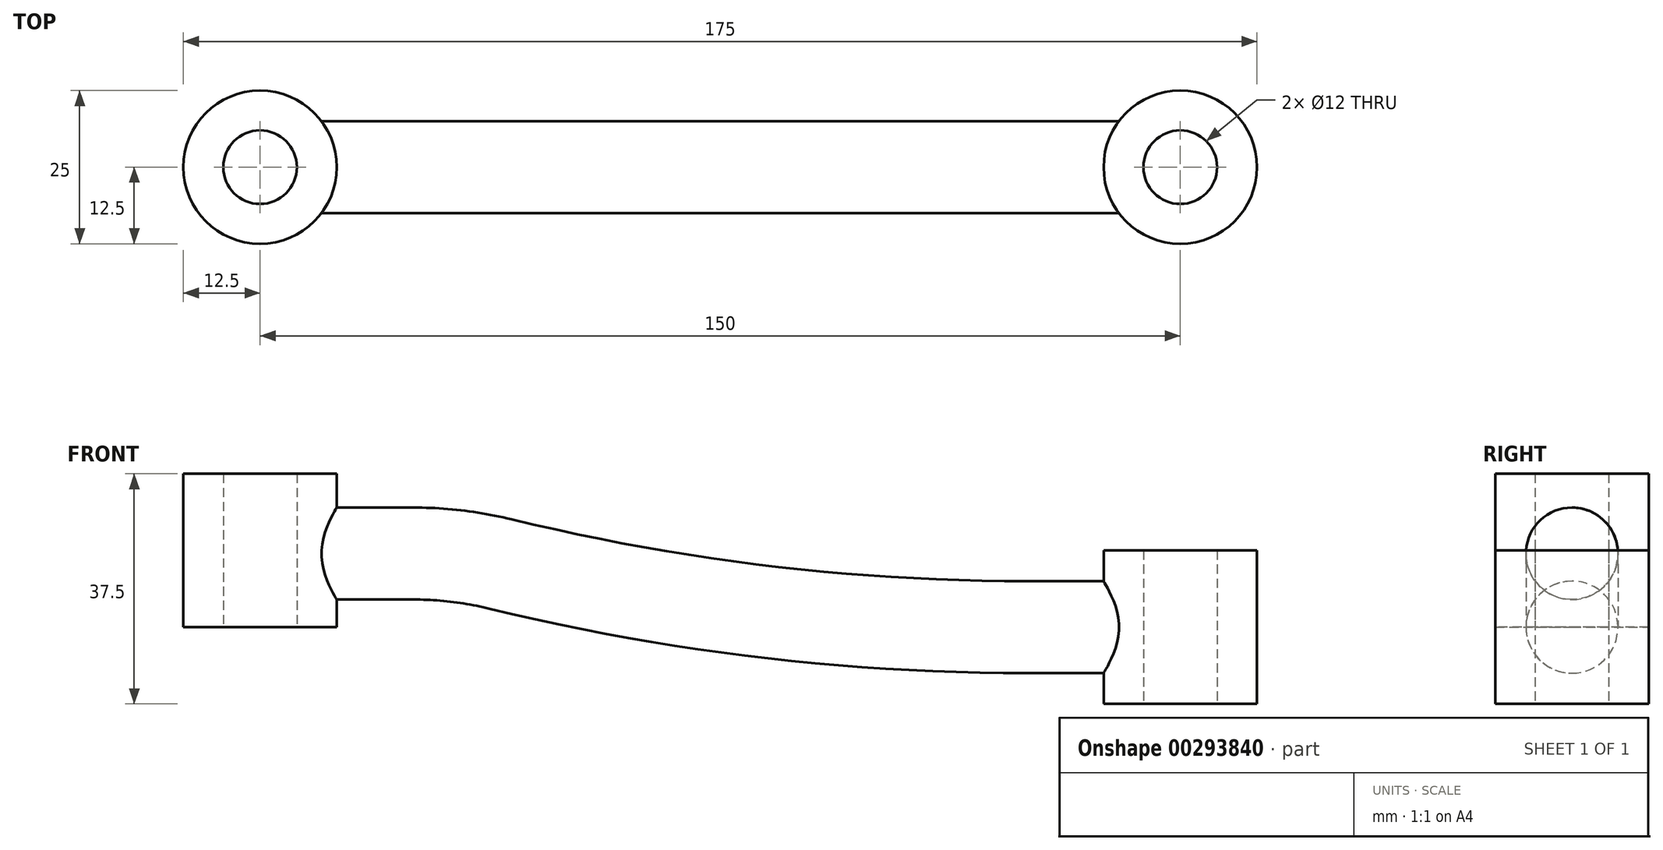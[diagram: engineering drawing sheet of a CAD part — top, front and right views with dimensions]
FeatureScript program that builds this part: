
annotation { "Feature Type Name" : "Feature", "Feature Type Description" : "" }
export const myFeature = defineFeature(function(context is Context, id is Id, definition is map)
    precondition{}
    {
        {
            var Q0;
            Q0=qCreatedBy(makeId("Top.planeOp"),FACE);
            var sketch = newSketch(context, id + "F0", { "sketchPlane" : qUnion([Q0])});
            skCircle(sketch, "E0", {"center": v(0, 0) * mm, "radius": 12.5 * mm});
            skCircle(sketch, "E1", {"center": v(150, 0) * mm, "radius": 12.5 * mm});
            skSolve(sketch);
        }
        {
            var Q0;
            Q0=makeQuery(id+"F0.imprint","IMPRINT",FACE,{"disambiguationData":[TD([[makeQuery(id+"F0.imprint","IMPRINT",EDGE,{"derivedFrom":sQuery(id+"F0.wireOp",EDGE,"E0")}),1.0]])]});
            extrude(context, id + "F1", {"entities" : qUnion([Q0]), "depth" : 25 * mm});
        }
        {
            var Q0;
            Q0=makeQuery(id+"F0.imprint","IMPRINT",FACE,{"disambiguationData":[TD([[makeQuery(id+"F0.imprint","IMPRINT",EDGE,{"derivedFrom":sQuery(id+"F0.wireOp",EDGE,"E1")}),1.0]])]});
            extrude(context, id + "F2", {"entities" : qUnion([Q0]), "endBound" : BoundingType.SYMMETRIC, "depth" : 25 * mm});
        }
        {
            var Q0;
            Q0=qCreatedBy(makeId("Front.planeOp"),FACE);
            var sketch = newSketch(context, id + "F3", { "sketchPlane" : qUnion([Q0])});
            skLineSegment(sketch, "E2", {"start": v(0, 12) * mm, "end": v(25, 12) * mm});
            skArc(sketch, "E3", {"start": v(25, 12) * mm, "mid": v(32.15, 11.57) * mm, "end": v(39.2, 10.3) * mm});
            skArc(sketch, "E4", {"start": v(39.2, 10.3) * mm, "mid": v(81.79, 2.58) * mm, "end": v(125, 0) * mm});
            skLineSegment(sketch, "E5", {"start": v(125, 0) * mm, "end": v(150, 0) * mm});
            skSolve(sketch);
        }
        {
            var Q0;
            Q0=qCreatedBy(makeId("Right.planeOp"),FACE);
            var sketch = newSketch(context, id + "F4", { "sketchPlane" : qUnion([Q0])});
            skCircle(sketch, "E6", {"center": v(0, 12) * mm, "radius": 7.5 * mm});
            skSolve(sketch);
        }
        {
            var Q0;
            Q0 = qSketchRegion(id + "F4", true);
            var Q1;
            Q1 = qConstructionFilter(qBodyType(qCreatedBy(id + "F3" ,EDGE), BodyType.WIRE), ConstructionObject.NO);
            sweep(context, id + "F5", {"operationType" : NewBodyOperationType.ADD, "profiles" : qUnion([Q0]), "path" : qUnion([Q1])});
        }
        {
            var Q0;
            Q0=qCreatedBy(makeId("Top.planeOp"),FACE);
            var sketch = newSketch(context, id + "F6", { "sketchPlane" : qUnion([Q0])});
            skCircle(sketch, "E7", {"center": v(0, 0) * mm, "radius": 6 * mm});
            skCircle(sketch, "E8", {"center": v(150, 0) * mm, "radius": 6 * mm});
            skSolve(sketch);
        }
        {
            var Q0;
            Q0 = qSketchRegion(id + "F6", true);
            extrude(context, id + "F7", {"entities" : qUnion([Q0]), "operationType" : NewBodyOperationType.REMOVE, "endBound" : BoundingType.THROUGH_ALL, "depth" : 25 * mm, "hasSecondDirection" : true, "secondDirectionBound" : SecondDirectionBoundingType.THROUGH_ALL, "secondDirectionOppositeDirection" : true, "secondDirectionDepth" : 25 * mm});
        }
    });
